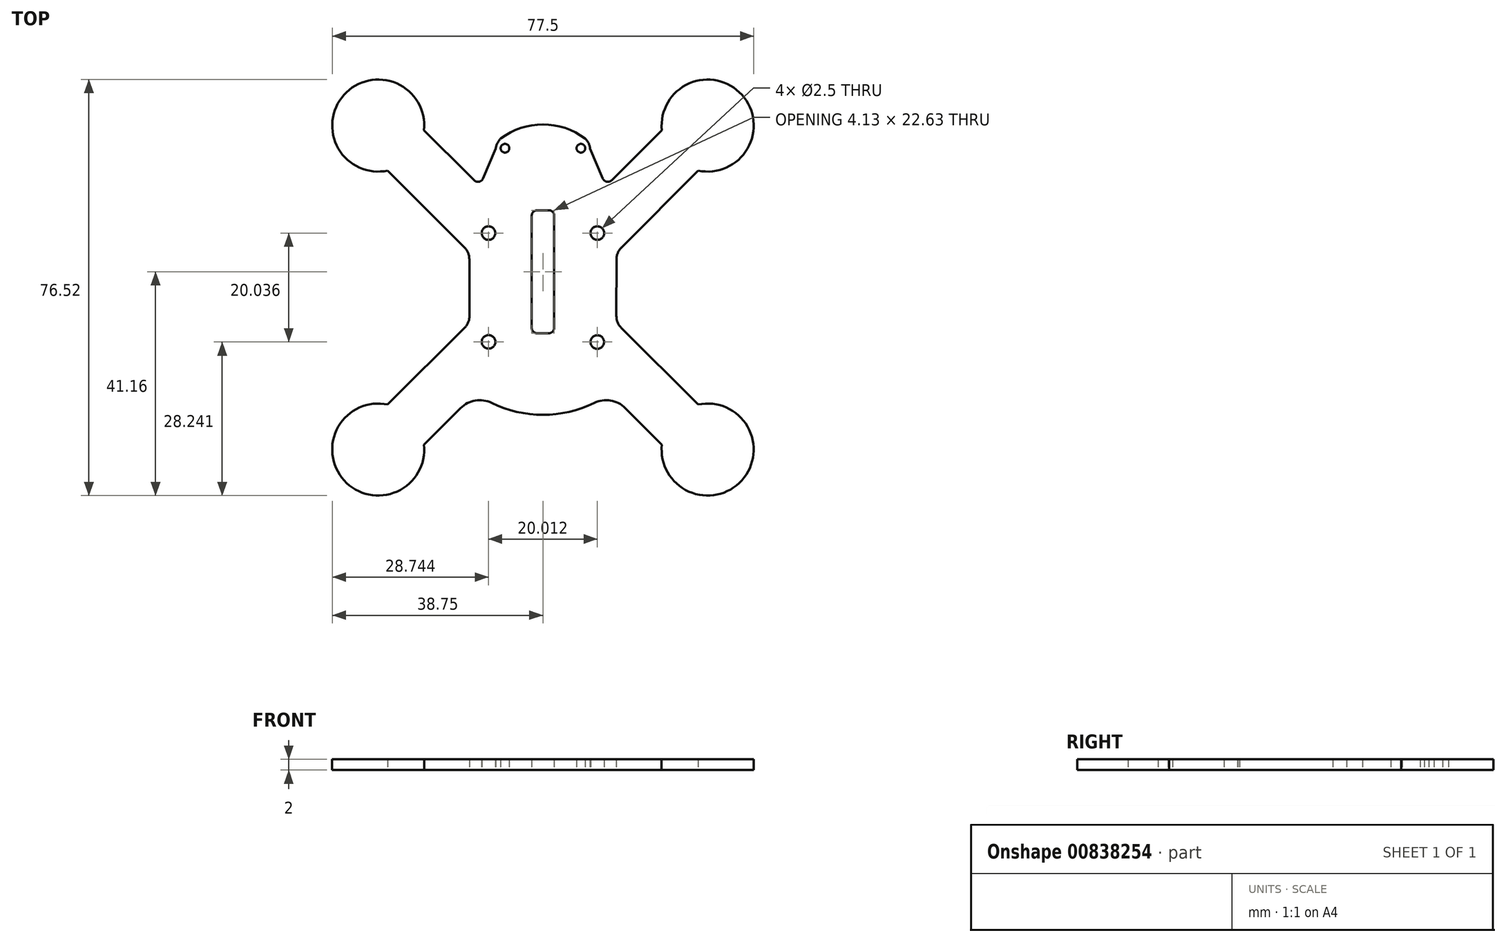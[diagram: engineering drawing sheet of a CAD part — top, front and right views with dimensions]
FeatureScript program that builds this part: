
annotation { "Feature Type Name" : "Feature", "Feature Type Description" : "" }
export const myFeature = defineFeature(function(context is Context, id is Id, definition is map)
    precondition{}
    {
        {
            var Q0;
            Q0=qCreatedBy(makeId("Top.planeOp"),FACE);
            var sketch = newSketch(context, id + "F0", { "sketchPlane" : qUnion([Q0])});
            skCircle(sketch, "E0.MirrorC", {"center": v(10, -5.4) * mm, "radius": 1.25 * mm});
            skPoint(sketch, "E1.left.start.orphan", {"position": v(10, -5.37) * mm});
            skCircle(sketch, "E2.MirrorC", {"center": v(-10, -5.37) * mm, "radius": 1.25 * mm});
            skCircle(sketch, "E3.MirrorC", {"center": v(-10, 14.64) * mm, "radius": 1.25 * mm});
            skLineSegment(sketch, "E4.MirrorCS", {"start": v(-6.98, 30.24) * mm, "end": v(-6.98, 28.02) * mm, "construction": true});
            skCircle(sketch, "E5.MirrorC", {"center": v(-6.98, 30.24) * mm, "radius": 0.8 * mm});
            skCircle(sketch, "E6.MirrorC", {"center": v(6.98, 30.24) * mm, "radius": 0.8 * mm});
            skLineSegment(sketch, "E7.MirrorCS", {"start": v(6.98, 30.24) * mm, "end": v(6.98, 28.02) * mm, "construction": true});
            skArc(sketch, "E8", {"start": v(-7.78, 32) * mm, "mid": v(-8.39, 31.17) * mm, "end": v(-8.68, 30.2) * mm});
            skArc(sketch, "E9.MirrorCS", {"start": v(7.78, 32) * mm, "mid": v(8.39, 31.17) * mm, "end": v(8.68, 30.2) * mm});
            skArc(sketch, "E10", {"start": v(7.78, 32) * mm, "mid": v(0, 34.63) * mm, "end": v(-7.78, 32) * mm});
            skLineSegment(sketch, "E11.bottom", {"start": v(-1.06, 18.84) * mm, "end": v(1.06, 18.84) * mm});
            skLineSegment(sketch, "E11.top", {"start": v(-1.06, -3.8) * mm, "end": v(1.06, -3.8) * mm});
            skLineSegment(sketch, "E11.left", {"start": v(-2.06, 17.84) * mm, "end": v(-2.06, -2.8) * mm});
            skLineSegment(sketch, "E11.right", {"start": v(2.06, 17.84) * mm, "end": v(2.06, -2.8) * mm});
            skPoint(sketch, "E11.middle", {"position": v(0, 7.52) * mm});
            skArc(sketch, "E12.filletArc", {"start": v(2.06, 17.84) * mm, "mid": v(1.77, 18.54) * mm, "end": v(1.06, 18.84) * mm});
            skPoint(sketch, "E13.visualSharp", {"position": v(-2.06, -3.8) * mm});
            skArc(sketch, "E13.filletArc", {"start": v(-2.06, -2.8) * mm, "mid": v(-1.77, -3.5) * mm, "end": v(-1.06, -3.8) * mm});
            skArc(sketch, "E14.filletArc", {"start": v(1.06, -3.8) * mm, "mid": v(1.77, -3.5) * mm, "end": v(2.06, -2.8) * mm});
            skPoint(sketch, "E15.visualSharp", {"position": v(-2.06, 18.84) * mm});
            skArc(sketch, "E15.filletArc", {"start": v(-1.06, 18.84) * mm, "mid": v(-1.77, 18.54) * mm, "end": v(-2.06, 17.84) * mm});
            skLineSegment(sketch, "E16.bottom", {"start": v(10, -5.4) * mm, "end": v(-10.01, -5.4) * mm, "construction": true});
            skLineSegment(sketch, "E17", {"start": v(-10, 14.64) * mm, "end": v(10, -5.4) * mm, "construction": true});
            skPoint(sketch, "E18", {"position": v(0, 4.62) * mm});
            skLineSegment(sketch, "E19", {"start": v(-10, 14.64) * mm, "end": v(-10.89, 13.75) * mm, "construction": true});
            skLineSegment(sketch, "E20", {"start": v(-14.41, 11.98) * mm, "end": v(-28.54, 26.13) * mm});
            skLineSegment(sketch, "E21", {"start": v(-10, 14.64) * mm, "end": v(-9.12, 15.52) * mm, "construction": true});
            skLineSegment(sketch, "E22", {"start": v(-12.65, 24.35) * mm, "end": v(-13.54, 25.25) * mm});
            skLineSegment(sketch, "E23", {"start": v(-13.54, 9.87) * mm, "end": v(-13.5, -0.63) * mm});
            skLineSegment(sketch, "E24.MirrorCS", {"start": v(13.54, 9.87) * mm, "end": v(13.5, -0.63) * mm});
            skLineSegment(sketch, "E25.MirrorCS", {"start": v(14.41, 11.98) * mm, "end": v(28.54, 26.13) * mm});
            skLineSegment(sketch, "E26", {"start": v(-8.68, 30.2) * mm, "end": v(-11.02, 24.67) * mm});
            skLineSegment(sketch, "E27.MirrorCS", {"start": v(8.68, 30.2) * mm, "end": v(11.02, 24.67) * mm});
            skPoint(sketch, "E28.orphan", {"position": v(-9.66, 21.37) * mm});
            skPoint(sketch, "E29.MirrorCS.end.orphan", {"position": v(8.68, 30.2) * mm});
            skPoint(sketch, "E29.MirrorCS.start.orphan", {"position": v(9.66, 21.37) * mm});
            skPoint(sketch, "E30.MirrorCS.end.orphan", {"position": v(13.54, 25.25) * mm});
            skLineSegment(sketch, "E31.MirrorCS", {"start": v(12.65, 24.35) * mm, "end": v(13.54, 25.25) * mm});
            skLineSegment(sketch, "E32", {"start": v(-14.39, -2.76) * mm, "end": v(-28.54, -16.9) * mm});
            skLineSegment(sketch, "E33.MirrorCS", {"start": v(14.39, -2.76) * mm, "end": v(28.54, -16.9) * mm});
            skLineSegment(sketch, "E34", {"start": v(0, 4.62) * mm, "end": v(-11.11, 4.62) * mm, "construction": true});
            skPoint(sketch, "E35.visualSharp", {"position": v(-13.5, -1.88) * mm});
            skArc(sketch, "E35.filletArc", {"start": v(-14.39, -2.76) * mm, "mid": v(-13.74, -1.79) * mm, "end": v(-13.5, -0.63) * mm});
            skPoint(sketch, "E36.visualSharp", {"position": v(-13.54, 11.1) * mm});
            skArc(sketch, "E36.filletArc", {"start": v(-13.54, 9.87) * mm, "mid": v(-13.77, 11) * mm, "end": v(-14.41, 11.98) * mm});
            skPoint(sketch, "E37.visualSharp", {"position": v(13.54, 11.1) * mm});
            skArc(sketch, "E37.filletArc", {"start": v(14.41, 11.98) * mm, "mid": v(13.77, 11) * mm, "end": v(13.54, 9.87) * mm});
            skPoint(sketch, "E38.visualSharp", {"position": v(13.5, -1.88) * mm});
            skArc(sketch, "E38.filletArc", {"start": v(13.5, -0.63) * mm, "mid": v(13.74, -1.79) * mm, "end": v(14.39, -2.76) * mm});
            skPoint(sketch, "E39.visualSharp", {"position": v(-11.6, 23.3) * mm});
            skArc(sketch, "E39.filletArc", {"start": v(-12.65, 24.35) * mm, "mid": v(-11.75, 24.08) * mm, "end": v(-11.02, 24.67) * mm});
            skPoint(sketch, "E40.visualSharp", {"position": v(11.6, 23.3) * mm});
            skArc(sketch, "E40.filletArc", {"start": v(11.02, 24.67) * mm, "mid": v(11.75, 24.08) * mm, "end": v(12.65, 24.35) * mm});
            skPoint(sketch, "E41", {"position": v(-13.52, 4.62) * mm});
            skLineSegment(sketch, "E42", {"start": v(-15.14, -17.56) * mm, "end": v(-21.87, -24.27) * mm});
            skLineSegment(sketch, "E43.MirrorCS", {"start": v(10, 14.64) * mm, "end": v(10.89, 13.75) * mm, "construction": true});
            skLineSegment(sketch, "E44.MirrorCS", {"start": v(10, 14.64) * mm, "end": v(9.12, 15.52) * mm, "construction": true});
            skCircle(sketch, "E45.MirrorC", {"center": v(10, 14.64) * mm, "radius": 1.25 * mm});
            skLineSegment(sketch, "E46", {"start": v(-13.54, 25.25) * mm, "end": v(-21.86, 33.58) * mm});
            skLineSegment(sketch, "E47", {"start": v(13.54, 25.25) * mm, "end": v(22.02, 33.74) * mm});
            skLineSegment(sketch, "E48.MirrorCS", {"start": v(15.14, -17.56) * mm, "end": v(21.87, -24.27) * mm});
            skArc(sketch, "E49", {"start": v(-28.54, -16.9) * mm, "mid": v(-36.56, -30.86) * mm, "end": v(-21.87, -24.27) * mm});
            skArc(sketch, "E50.MirrorCS", {"start": v(28.54, -16.9) * mm, "mid": v(36.56, -30.86) * mm, "end": v(21.87, -24.27) * mm});
            skLineSegment(sketch, "E51.MirrorCS", {"start": v(0, 4.62) * mm, "end": v(11.11, 4.62) * mm, "construction": true});
            skArc(sketch, "E52.MirrorCS", {"start": v(-28.54, 26.13) * mm, "mid": v(-36.59, 40.07) * mm, "end": v(-21.86, 33.58) * mm});
            skArc(sketch, "E53.MirrorCS", {"start": v(28.54, 26.13) * mm, "mid": v(36.56, 40.1) * mm, "end": v(21.87, 33.5) * mm});
            skPoint(sketch, "E54.orphan", {"position": v(9.13, -11.55) * mm});
            skPoint(sketch, "E55.orphan", {"position": v(-9.13, -11.55) * mm});
            skPoint(sketch, "E56.visualSharp", {"position": v(-10.94, -13.36) * mm});
            skPoint(sketch, "E57.visualSharp", {"position": v(10.94, -13.36) * mm});
            skArc(sketch, "E58", {"start": v(-9.41, -16.6) * mm, "mid": v(0, -18.79) * mm, "end": v(9.41, -16.6) * mm});
            skPoint(sketch, "E59.visualSharp", {"position": v(12.4, -14.82) * mm});
            skArc(sketch, "E59.filletArc", {"start": v(15.14, -17.56) * mm, "mid": v(12.43, -16.16) * mm, "end": v(9.41, -16.6) * mm});
            skPoint(sketch, "E60.visualSharp", {"position": v(-12.4, -14.82) * mm});
            skArc(sketch, "E60.filletArc", {"start": v(-9.41, -16.6) * mm, "mid": v(-12.43, -16.16) * mm, "end": v(-15.14, -17.56) * mm});
            skLineSegment(sketch, "E61", {"start": v(-21.86, 33.58) * mm, "end": v(-26.2, 41.84) * mm});
            skLineSegment(sketch, "E62.MirrorCS", {"start": v(-28.93, 26.52) * mm, "end": v(-37.18, 30.89) * mm});
            skSolve(sketch);
        }
        {
            var Q0;
            Q0 = qSketchRegion(id + "F0", true);
            extrude(context, id + "F1", {"entities" : qUnion([Q0]), "depth" : 2 * mm, "offsetDistance" : 25 * mm});
        }
    });
